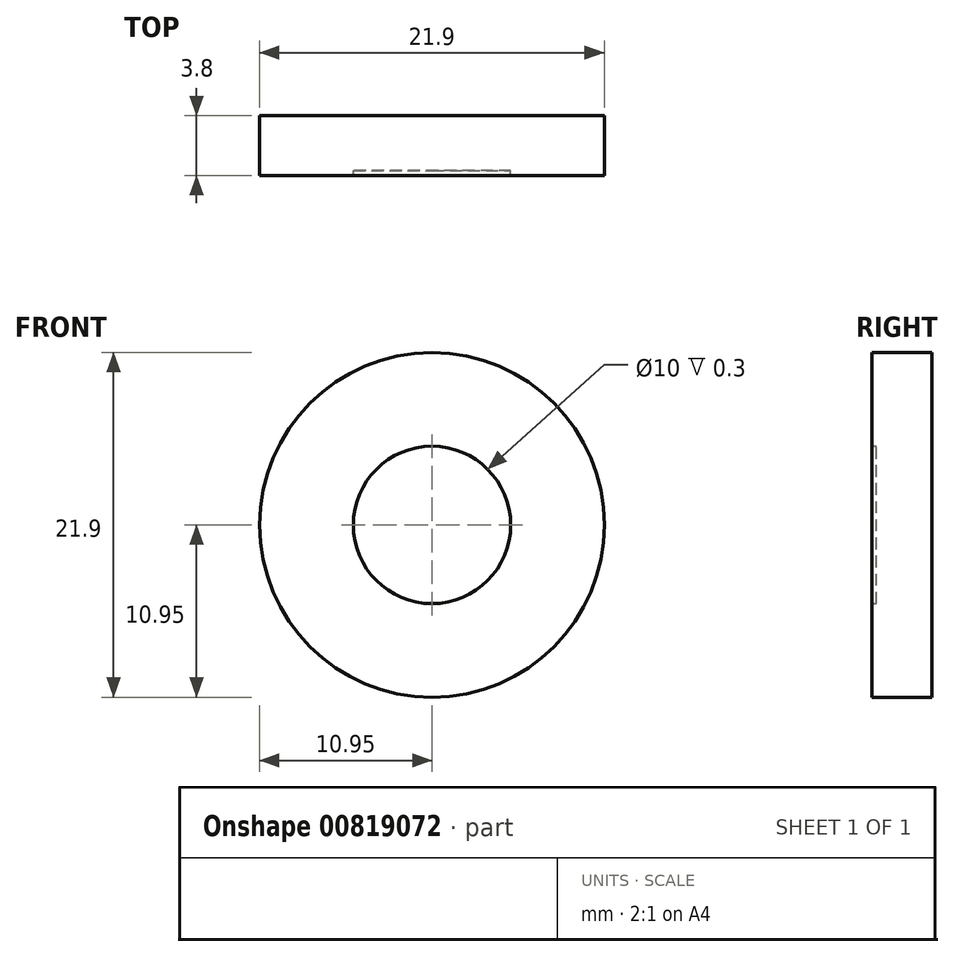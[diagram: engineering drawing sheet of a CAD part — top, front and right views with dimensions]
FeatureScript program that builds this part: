
annotation { "Feature Type Name" : "Feature", "Feature Type Description" : "" }
export const myFeature = defineFeature(function(context is Context, id is Id, definition is map)
    precondition{}
    {
        {
            var Q0;
            Q0=qCreatedBy(makeId("Front.planeOp"),FACE);
            var sketch = newSketch(context, id + "F0", { "sketchPlane" : qUnion([Q0])});
            skCircle(sketch, "E0", {"center": v(0, 0) * mm, "radius": 10.95 * mm});
            skCircle(sketch, "E1", {"center": v(0, 0) * mm, "radius": 5 * mm});
            skSolve(sketch);
        }
        {
            var Q0;
            Q0 = qSketchRegion(id + "F0", true);
            extrude(context, id + "F1", {"entities" : qUnion([Q0]), "depth" : 3.8 * mm, "offsetDistance" : 25 * mm});
        }
        {
            var Q0;
            Q0=makeQuery(id+"F0.imprint","IMPRINT",FACE,{"disambiguationData":[TD([[makeQuery(id+"F0.imprint","IMPRINT",EDGE,{"derivedFrom":sQuery(id+"F0.wireOp",EDGE,"E1")}),1.0]])]});
            extrude(context, id + "F2", {"entities" : qUnion([Q0]), "operationType" : NewBodyOperationType.ADD, "depth" : 3.5 * mm, "offsetDistance" : 25 * mm});
        }
    });
